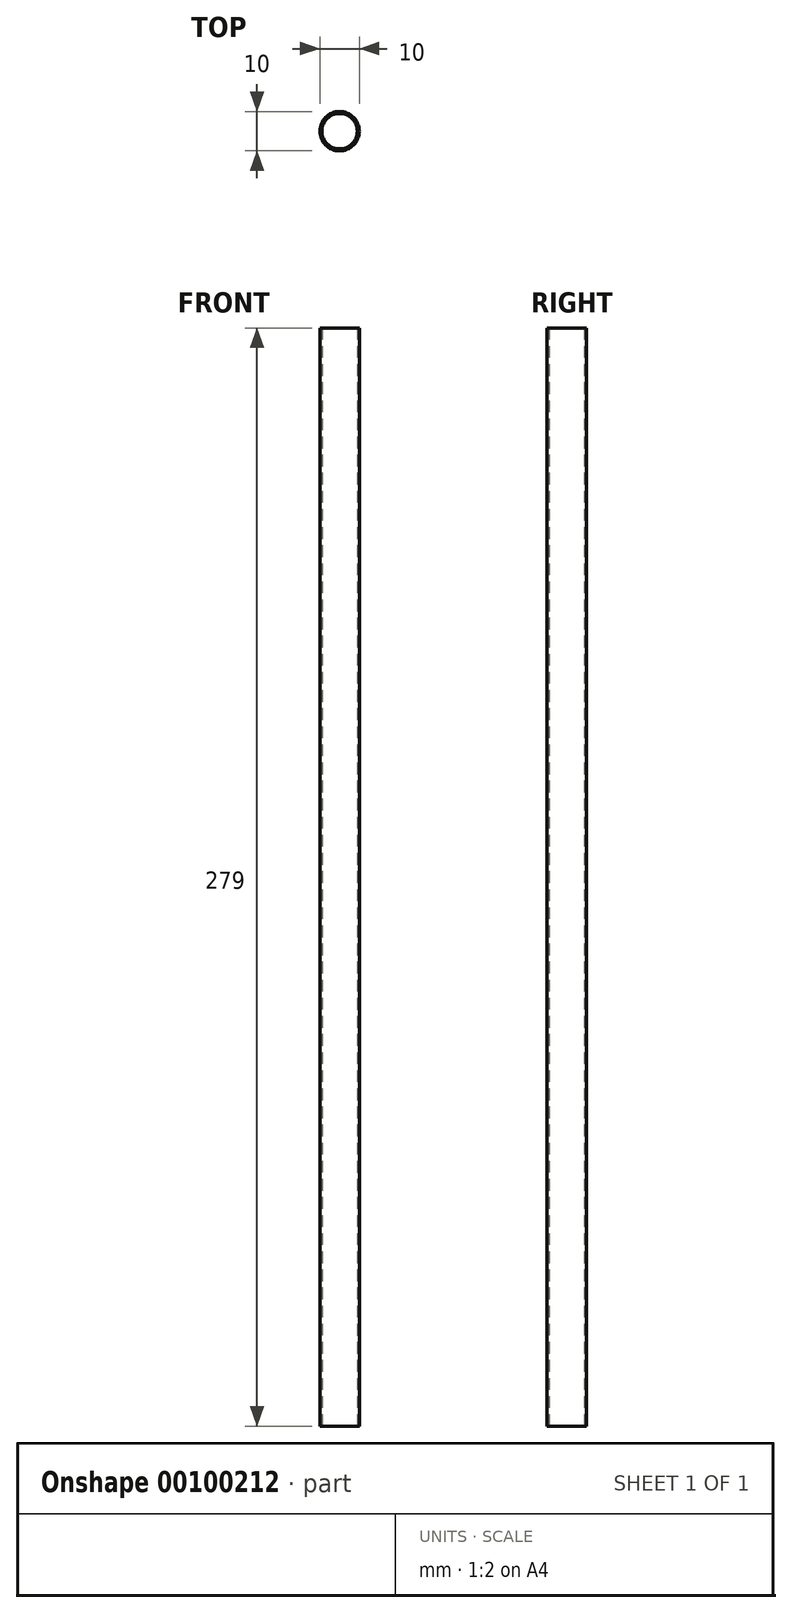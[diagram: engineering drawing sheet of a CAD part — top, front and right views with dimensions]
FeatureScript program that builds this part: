
annotation { "Feature Type Name" : "Feature", "Feature Type Description" : "" }
export const myFeature = defineFeature(function(context is Context, id is Id, definition is map)
    precondition{}
    {
        {
            var Q0;
            Q0=qCreatedBy(makeId("Top.planeOp"),FACE);
            var sketch = newSketch(context, id + "F0", { "sketchPlane" : qUnion([Q0])});
            skCircle(sketch, "E0", {"center": v(0, 0) * mm, "radius": 5 * mm});
            skSolve(sketch);
        }
        {
            var Q0;
            Q0=qCreatedBy(makeId("Top.planeOp"),FACE);
            var sketch = newSketch(context, id + "F1", { "sketchPlane" : qUnion([Q0])});
            skCircle(sketch, "E1", {"center": v(0, 0) * mm, "radius": 4.5 * mm});
            skSolve(sketch);
        }
        {
            var Q0;
            Q0 = qSketchRegion(id + "F1", true);
            var Q1;
            Q1=makeQuery(id+"F0.imprint","IMPRINT",FACE,{"disambiguationData":[TD([[makeQuery(id+"F0.imprint","IMPRINT",EDGE,{"derivedFrom":sQuery(id+"F0.wireOp",EDGE,"E0")}),1.0]])]});
            extrude(context, id + "F2", {"entities" : qUnion([Q0, Q1]), "depth" : 279 * mm});
        }
    });
